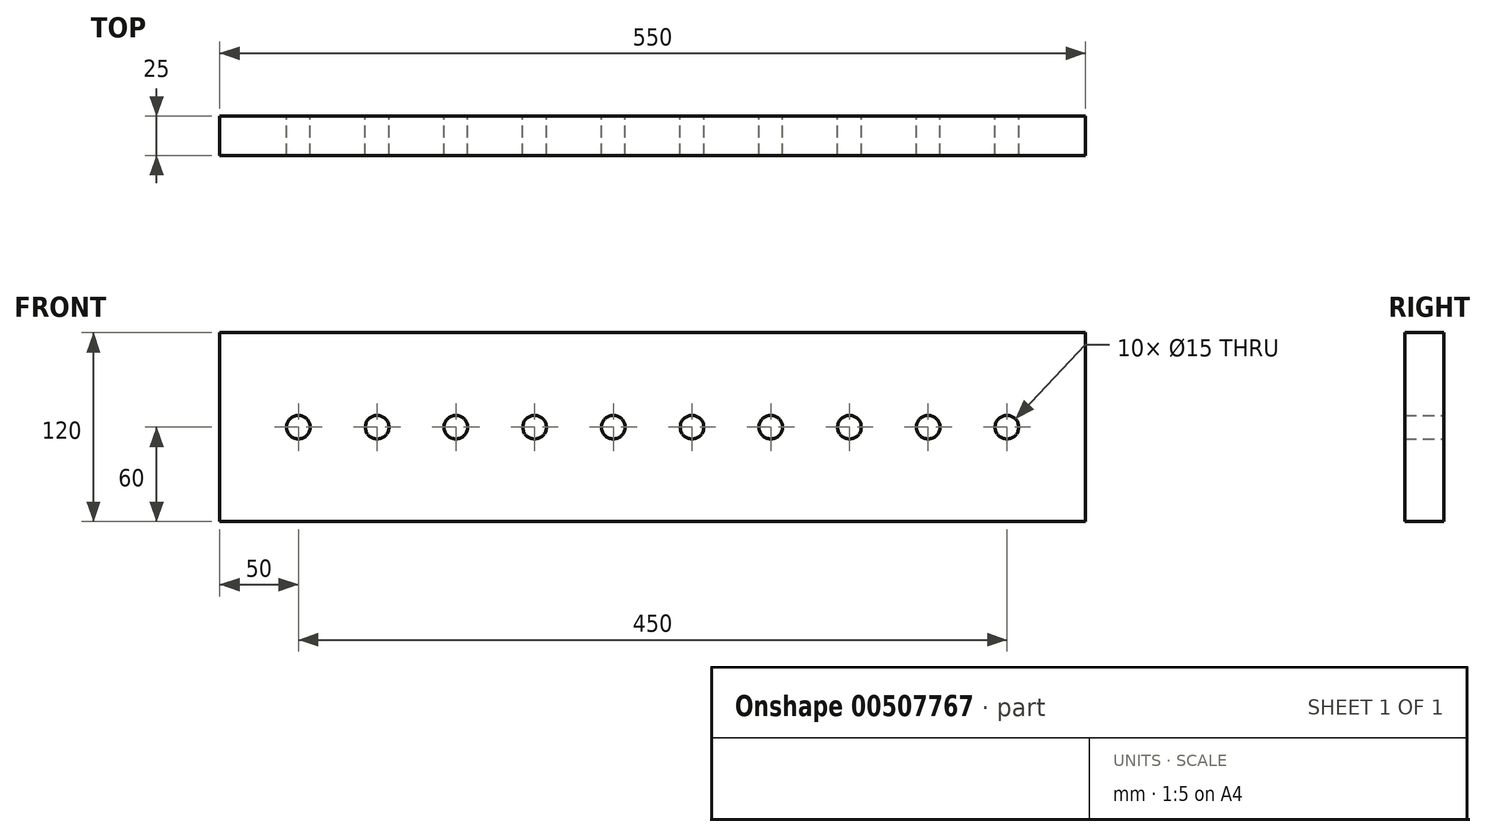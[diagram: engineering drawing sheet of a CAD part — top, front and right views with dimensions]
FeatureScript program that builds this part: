
annotation { "Feature Type Name" : "Feature", "Feature Type Description" : "" }
export const myFeature = defineFeature(function(context is Context, id is Id, definition is map)
    precondition{}
    {
        {
            var Q0;
            Q0=qCreatedBy(makeId("Front.planeOp"),FACE);
            var sketch = newSketch(context, id + "F0", { "sketchPlane" : qUnion([Q0])});
            skCircle(sketch, "E0", {"center": v(-50, 0) * mm, "radius": 7.5 * mm});
            skCircle(sketch, "E1.1.0.0", {"center": v(0, 0) * mm, "radius": 7.5 * mm});
            skCircle(sketch, "E1.2.0.0", {"center": v(50, 0) * mm, "radius": 7.5 * mm});
            skCircle(sketch, "E1.3.0.0", {"center": v(100, 0) * mm, "radius": 7.5 * mm});
            skCircle(sketch, "E1.4.0.0", {"center": v(150, 0) * mm, "radius": 7.5 * mm});
            skCircle(sketch, "E1.5.0.0", {"center": v(200, 0) * mm, "radius": 7.5 * mm});
            skCircle(sketch, "E1.6.0.0", {"center": v(250, 0) * mm, "radius": 7.5 * mm});
            skCircle(sketch, "E1.7.0.0", {"center": v(300, 0) * mm, "radius": 7.5 * mm});
            skCircle(sketch, "E1.8.0.0", {"center": v(350, 0) * mm, "radius": 7.5 * mm});
            skCircle(sketch, "E1.9.0.0", {"center": v(400, 0) * mm, "radius": 7.5 * mm});
            skLineSegment(sketch, "E1.direction1", {"start": v(-50, 0) * mm, "end": v(0, 0) * mm, "construction": true});
            skLineSegment(sketch, "E2.bottom", {"start": v(-100, 60) * mm, "end": v(450, 60) * mm});
            skLineSegment(sketch, "E2.top", {"start": v(-100, -60) * mm, "end": v(450, -60) * mm});
            skLineSegment(sketch, "E2.left", {"start": v(-100, 60) * mm, "end": v(-100, -60) * mm});
            skLineSegment(sketch, "E2.right", {"start": v(450, 60) * mm, "end": v(450, -60) * mm});
            skSolve(sketch);
        }
        {
            var Q0;
            Q0=makeQuery(id+"F0.imprint","IMPRINT",FACE,{"disambiguationData":[TD([[makeQuery(id+"F0.imprint","IMPRINT",EDGE,{"derivedFrom":sQuery(id+"F0.wireOp",EDGE,"E0")}),-1.0]])]});
            extrude(context, id + "F1", {"entities" : qUnion([Q0]), "depth" : 25 * mm});
        }
    });
